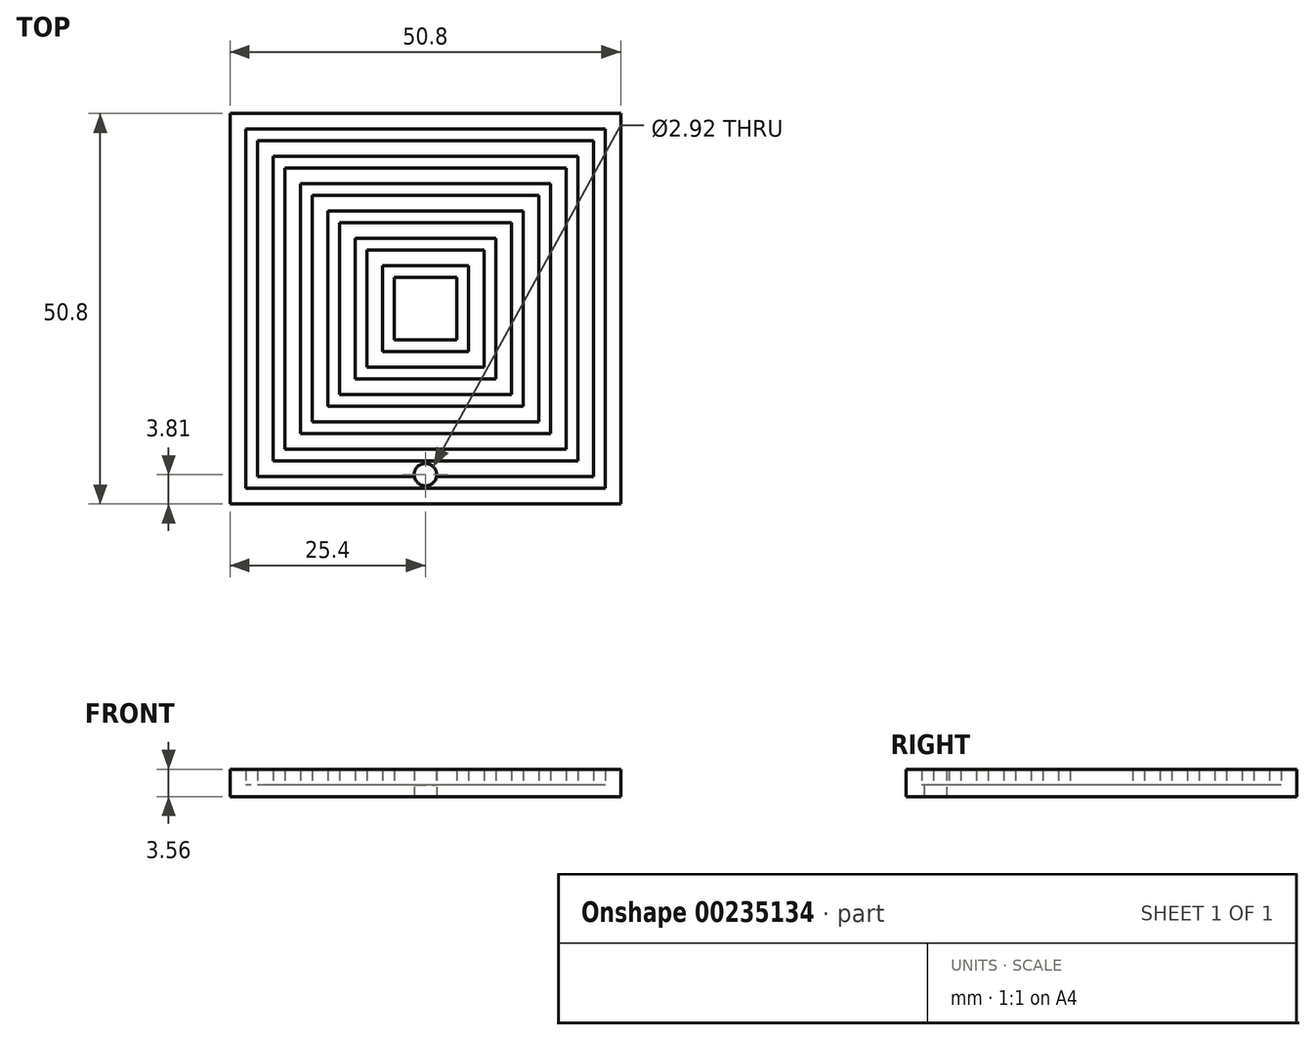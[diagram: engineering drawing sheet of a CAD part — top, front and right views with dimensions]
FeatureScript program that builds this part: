
annotation { "Feature Type Name" : "Feature", "Feature Type Description" : "" }
export const myFeature = defineFeature(function(context is Context, id is Id, definition is map)
    precondition{}
    {
        {
            var Q0;
            Q0=qCreatedBy(makeId("Top.planeOp"),FACE);
            var sketch = newSketch(context, id + "F0", { "sketchPlane" : qUnion([Q0])});
            skLineSegment(sketch, "E0.bottom", {"start": v(0, 0) * mm, "end": v(-50.8, 0) * mm});
            skLineSegment(sketch, "E0.top", {"start": v(0, 50.8) * mm, "end": v(-50.8, 50.8) * mm});
            skLineSegment(sketch, "E0.left", {"start": v(0, 0) * mm, "end": v(0, 50.8) * mm});
            skLineSegment(sketch, "E0.right", {"start": v(-50.8, 0) * mm, "end": v(-50.8, 50.8) * mm});
            skSolve(sketch);
        }
        {
            var Q0;
            Q0=makeQuery(id+"F0.imprint","IMPRINT",FACE,{"disambiguationData":[TD([[makeQuery(id+"F0.imprint","IMPRINT",EDGE,{"derivedFrom":sQuery(id+"F0.wireOp",EDGE,"E0.bottom")}),-1.0]])]});
            extrude(context, id + "F1", {"entities" : qUnion([Q0]), "depth" : 1.52 * mm});
        }
        {
            var Q0;
            {var subQ0=sQuery(id+"F0.wireOp",EDGE,"E0.bottom");var subQ1=sQuery(id+"F0.wireOp",EDGE,"E0.top");var subQ2=sQuery(id+"F0.wireOp",EDGE,"E0.right");var subQ3=sQuery(id+"F0.wireOp",EDGE,"E0.left");Q0=makeQuery(id+"FENrJbx9LFUyqxS_1.boolean.opBoolean","SPLIT",FACE,{"disambiguationData":[TD([makeQuery(id+"F1.opExtrude","SWEPT_FACE",FACE,{"disambiguationData":[OSD([subQ0])]})])],"derivedFrom":makeQuery(id+"F1.opExtrude","CAP_FACE",FACE,{"disambiguationData":[OSD([subQ0,subQ1,subQ3,subQ2])],"isStart":false})});}
            var sketch = newSketch(context, id + "F2", { "sketchPlane" : qUnion([Q0])});
            skLineSegment(sketch, "E1.bottom", {"start": v(-50.8, 50.8) * mm, "end": v(0, 50.8) * mm});
            skLineSegment(sketch, "E1.top", {"start": v(-50.8, 0) * mm, "end": v(0, 0) * mm});
            skLineSegment(sketch, "E1.left", {"start": v(-50.8, 50.8) * mm, "end": v(-50.8, 0) * mm});
            skLineSegment(sketch, "E1.right", {"start": v(0, 50.8) * mm, "end": v(0, 0) * mm});
            skLineSegment(sketch, "E2", {"start": v(-25.4, 50.8) * mm, "end": v(-25.4, 0) * mm, "construction": true});
            skLineSegment(sketch, "E3", {"start": v(-50.8, 25.4) * mm, "end": v(0, 25.4) * mm, "construction": true});
            skLineSegment(sketch, "E4.bottom", {"start": v(-2.03, 48.77) * mm, "end": v(-48.77, 48.77) * mm});
            skLineSegment(sketch, "E4.top", {"start": v(-2.03, 2.03) * mm, "end": v(-48.77, 2.03) * mm});
            skLineSegment(sketch, "E4.left", {"start": v(-2.03, 48.77) * mm, "end": v(-2.03, 2.03) * mm});
            skLineSegment(sketch, "E4.right", {"start": v(-48.77, 48.77) * mm, "end": v(-48.77, 2.03) * mm});
            skPoint(sketch, "E4.middle", {"position": v(-25.4, 25.4) * mm});
            skLineSegment(sketch, "E5.bottom", {"start": v(-3.56, 47.24) * mm, "end": v(-47.24, 47.24) * mm});
            skLineSegment(sketch, "E5.top", {"start": v(-3.56, 3.56) * mm, "end": v(-47.24, 3.56) * mm});
            skLineSegment(sketch, "E5.left", {"start": v(-3.56, 47.24) * mm, "end": v(-3.56, 3.56) * mm});
            skLineSegment(sketch, "E5.right", {"start": v(-47.24, 47.24) * mm, "end": v(-47.24, 3.56) * mm});
            skLineSegment(sketch, "E6.bottom", {"start": v(-5.59, 45.21) * mm, "end": v(-45.21, 45.21) * mm});
            skLineSegment(sketch, "E6.top", {"start": v(-5.59, 5.59) * mm, "end": v(-45.21, 5.59) * mm});
            skLineSegment(sketch, "E6.left", {"start": v(-5.59, 45.21) * mm, "end": v(-5.59, 5.59) * mm});
            skLineSegment(sketch, "E6.right", {"start": v(-45.21, 45.21) * mm, "end": v(-45.21, 5.59) * mm});
            skLineSegment(sketch, "E7.bottom", {"start": v(-7.11, 43.69) * mm, "end": v(-43.69, 43.69) * mm});
            skLineSegment(sketch, "E7.top", {"start": v(-7.11, 7.11) * mm, "end": v(-43.69, 7.11) * mm});
            skLineSegment(sketch, "E7.left", {"start": v(-7.11, 43.69) * mm, "end": v(-7.11, 7.11) * mm});
            skLineSegment(sketch, "E7.right", {"start": v(-43.69, 43.69) * mm, "end": v(-43.69, 7.11) * mm});
            skLineSegment(sketch, "E8.bottom", {"start": v(-9.14, 41.66) * mm, "end": v(-41.66, 41.66) * mm});
            skLineSegment(sketch, "E8.top", {"start": v(-9.14, 9.14) * mm, "end": v(-41.66, 9.14) * mm});
            skLineSegment(sketch, "E8.left", {"start": v(-9.14, 41.66) * mm, "end": v(-9.14, 9.14) * mm});
            skLineSegment(sketch, "E8.right", {"start": v(-41.66, 41.66) * mm, "end": v(-41.66, 9.14) * mm});
            skLineSegment(sketch, "E9.bottom", {"start": v(-10.67, 40.13) * mm, "end": v(-40.13, 40.13) * mm});
            skLineSegment(sketch, "E9.top", {"start": v(-10.67, 10.67) * mm, "end": v(-40.13, 10.67) * mm});
            skLineSegment(sketch, "E9.left", {"start": v(-10.67, 40.13) * mm, "end": v(-10.67, 10.67) * mm});
            skLineSegment(sketch, "E9.right", {"start": v(-40.13, 40.13) * mm, "end": v(-40.13, 10.67) * mm});
            skLineSegment(sketch, "E10.bottom", {"start": v(-12.7, 38.1) * mm, "end": v(-38.1, 38.1) * mm});
            skLineSegment(sketch, "E10.top", {"start": v(-12.7, 12.7) * mm, "end": v(-38.1, 12.7) * mm});
            skLineSegment(sketch, "E10.left", {"start": v(-12.7, 38.1) * mm, "end": v(-12.7, 12.7) * mm});
            skLineSegment(sketch, "E10.right", {"start": v(-38.1, 38.1) * mm, "end": v(-38.1, 12.7) * mm});
            skLineSegment(sketch, "E11.bottom", {"start": v(-14.22, 36.58) * mm, "end": v(-36.58, 36.58) * mm});
            skLineSegment(sketch, "E11.top", {"start": v(-14.22, 14.22) * mm, "end": v(-36.58, 14.22) * mm});
            skLineSegment(sketch, "E11.left", {"start": v(-14.22, 36.58) * mm, "end": v(-14.22, 14.22) * mm});
            skLineSegment(sketch, "E11.right", {"start": v(-36.58, 36.58) * mm, "end": v(-36.58, 14.22) * mm});
            skLineSegment(sketch, "E12.bottom", {"start": v(-16.26, 34.54) * mm, "end": v(-34.54, 34.54) * mm});
            skLineSegment(sketch, "E12.top", {"start": v(-16.26, 16.26) * mm, "end": v(-34.54, 16.26) * mm});
            skLineSegment(sketch, "E12.left", {"start": v(-16.26, 34.54) * mm, "end": v(-16.26, 16.26) * mm});
            skLineSegment(sketch, "E12.right", {"start": v(-34.54, 34.54) * mm, "end": v(-34.54, 16.26) * mm});
            skLineSegment(sketch, "E13.bottom", {"start": v(-17.78, 33.02) * mm, "end": v(-33.02, 33.02) * mm});
            skLineSegment(sketch, "E13.top", {"start": v(-17.78, 17.78) * mm, "end": v(-33.02, 17.78) * mm});
            skLineSegment(sketch, "E13.left", {"start": v(-17.78, 33.02) * mm, "end": v(-17.78, 17.78) * mm});
            skLineSegment(sketch, "E13.right", {"start": v(-33.02, 33.02) * mm, "end": v(-33.02, 17.78) * mm});
            skLineSegment(sketch, "E14.bottom", {"start": v(-19.81, 19.81) * mm, "end": v(-30.99, 19.81) * mm});
            skLineSegment(sketch, "E14.top", {"start": v(-19.81, 30.99) * mm, "end": v(-30.99, 30.99) * mm});
            skLineSegment(sketch, "E14.left", {"start": v(-19.81, 30.99) * mm, "end": v(-19.81, 19.81) * mm});
            skLineSegment(sketch, "E14.right", {"start": v(-30.99, 30.99) * mm, "end": v(-30.99, 19.81) * mm});
            skLineSegment(sketch, "E15.bottom", {"start": v(-21.34, 29.46) * mm, "end": v(-29.46, 29.46) * mm});
            skLineSegment(sketch, "E15.top", {"start": v(-21.34, 21.34) * mm, "end": v(-29.46, 21.34) * mm});
            skLineSegment(sketch, "E15.left", {"start": v(-21.34, 29.46) * mm, "end": v(-21.34, 21.34) * mm});
            skLineSegment(sketch, "E15.right", {"start": v(-29.46, 29.46) * mm, "end": v(-29.46, 21.34) * mm});
            skSolve(sketch);
        }
        {
            var Q0;
            Q0=makeQuery(id+"F2.imprint","IMPRINT",FACE,{"disambiguationData":[TD([[makeQuery(id+"F2.imprint","IMPRINT",EDGE,{"derivedFrom":sQuery(id+"F2.wireOp",EDGE,"E1.bottom")}),1.0]])]});
            var Q1;
            Q1=makeQuery(id+"F2.imprint","IMPRINT",FACE,{"disambiguationData":[TD([[makeQuery(id+"F2.imprint","IMPRINT",EDGE,{"derivedFrom":sQuery(id+"F2.wireOp",EDGE,"E5.bottom")}),1.0]])]});
            var Q2;
            Q2=makeQuery(id+"F2.imprint","IMPRINT",FACE,{"disambiguationData":[TD([[makeQuery(id+"F2.imprint","IMPRINT",EDGE,{"derivedFrom":sQuery(id+"F2.wireOp",EDGE,"E7.bottom")}),1.0]])]});
            var Q3;
            Q3=makeQuery(id+"F2.imprint","IMPRINT",FACE,{"disambiguationData":[TD([[makeQuery(id+"F2.imprint","IMPRINT",EDGE,{"derivedFrom":sQuery(id+"F2.wireOp",EDGE,"E9.bottom")}),1.0]])]});
            var Q4;
            Q4=makeQuery(id+"F2.imprint","IMPRINT",FACE,{"disambiguationData":[TD([[makeQuery(id+"F2.imprint","IMPRINT",EDGE,{"derivedFrom":sQuery(id+"F2.wireOp",EDGE,"E11.bottom")}),1.0]])]});
            var Q5;
            Q5=makeQuery(id+"F2.imprint","IMPRINT",FACE,{"disambiguationData":[TD([[makeQuery(id+"F2.imprint","IMPRINT",EDGE,{"derivedFrom":sQuery(id+"F2.wireOp",EDGE,"E13.bottom")}),1.0]])]});
            var Q6;
            Q6=makeQuery(id+"F2.imprint","IMPRINT",FACE,{"disambiguationData":[TD([[makeQuery(id+"F2.imprint","IMPRINT",EDGE,{"derivedFrom":sQuery(id+"F2.wireOp",EDGE,"E15.bottom")}),1.0]])]});
            extrude(context, id + "F3", {"entities" : qUnion([Q0, Q1, Q2, Q3, Q4, Q5, Q6]), "operationType" : NewBodyOperationType.ADD, "depth" : 2.03 * mm});
        }
        {
            var Q0;
            Q0=makeQuery(id+"F1.opExtrude","CAP_FACE",FACE,{"disambiguationData":[OSD([sQuery(id+"F0.wireOp",EDGE,"E0.bottom"),sQuery(id+"F0.wireOp",EDGE,"E0.top"),sQuery(id+"F0.wireOp",EDGE,"E0.left"),sQuery(id+"F0.wireOp",EDGE,"E0.right")])],"isStart":true});
            var sketch = newSketch(context, id + "F4", { "sketchPlane" : qUnion([Q0])});
            skCircle(sketch, "E16", {"center": v(-25.4, -3.81) * mm, "radius": 1.46 * mm});
            skSolve(sketch);
        }
        {
            var Q0;
            Q0=makeQuery(id+"F4.imprint","IMPRINT",FACE,{"disambiguationData":[TD([[makeQuery(id+"F4.imprint","IMPRINT",EDGE,{"derivedFrom":sQuery(id+"F4.wireOp",EDGE,"E16")}),1.0]])]});
            extrude(context, id + "F5", {"entities" : qUnion([Q0]), "operationType" : NewBodyOperationType.REMOVE, "oppositeDirection" : true, "depth" : 25.4 * mm});
        }
    });
